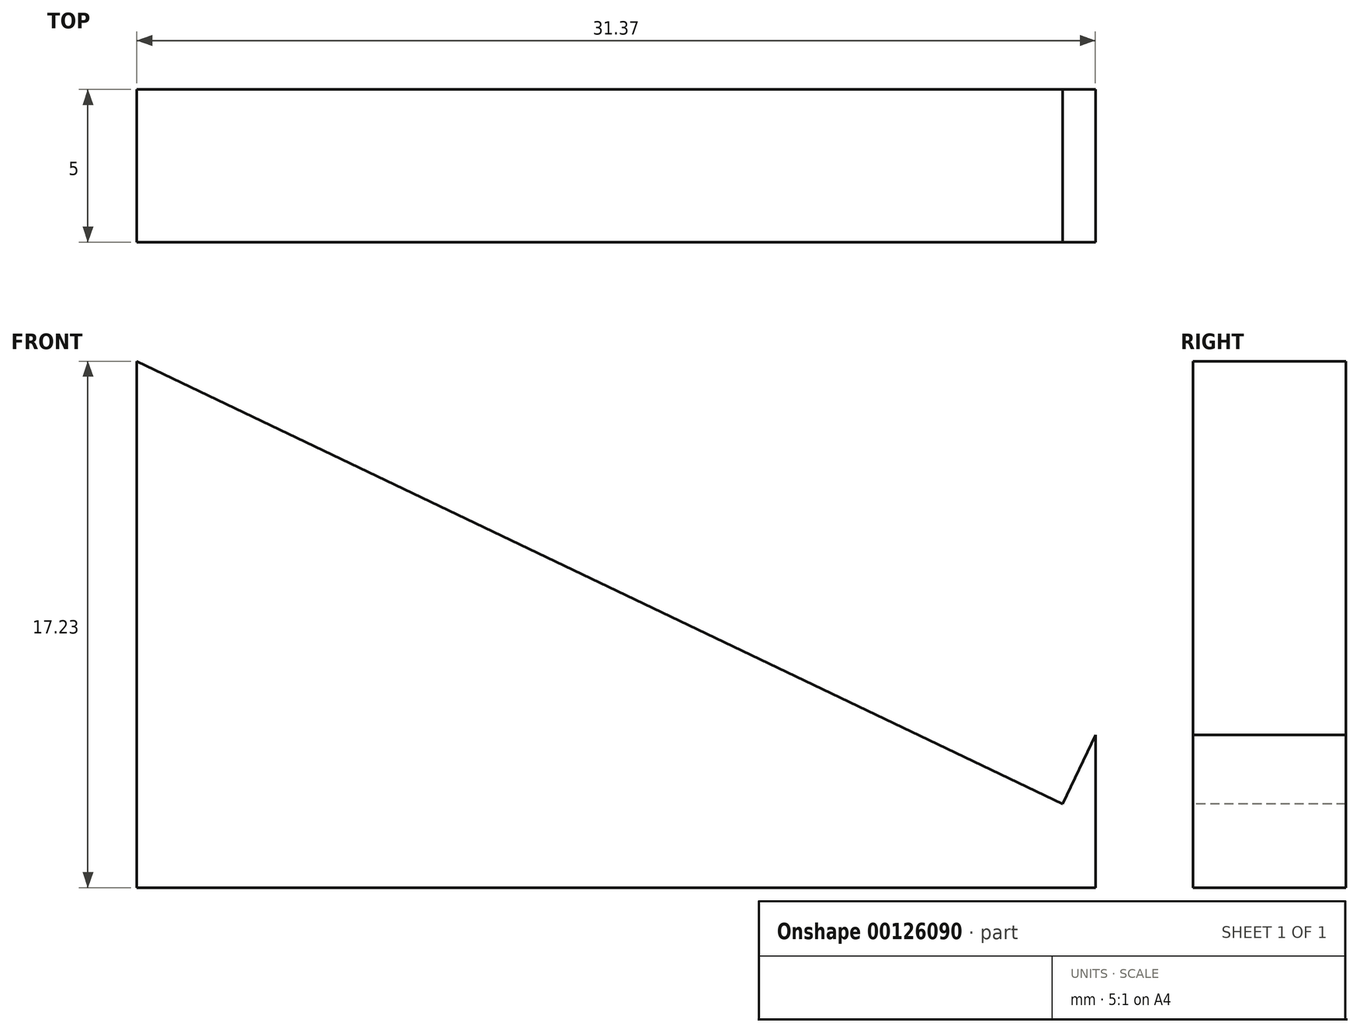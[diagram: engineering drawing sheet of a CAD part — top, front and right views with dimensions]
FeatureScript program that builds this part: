
annotation { "Feature Type Name" : "Feature", "Feature Type Description" : "" }
export const myFeature = defineFeature(function(context is Context, id is Id, definition is map)
    precondition{}
    {
        {
            var Q0;
            Q0=qCreatedBy(makeId("Front.planeOp"),FACE);
            var sketch = newSketch(context, id + "F0", { "sketchPlane" : qUnion([Q0])});
            skLineSegment(sketch, "E0", {"start": v(0, 0) * mm, "end": v(31.37, 0) * mm});
            skLineSegment(sketch, "E1", {"start": v(31.37, 0) * mm, "end": v(31.37, 5) * mm});
            skLineSegment(sketch, "E2", {"start": v(31.37, 5) * mm, "end": v(0, 20) * mm});
            skLineSegment(sketch, "E3", {"start": v(0, 20) * mm, "end": v(0, 0) * mm});
            skSolve(sketch);
        }
        {
            var Q0;
            Q0 = qSketchRegion(id + "F0", true);
            extrude(context, id + "F1", {"entities" : qUnion([Q0]), "oppositeDirection" : true, "depth" : 5 * mm});
        }
        {
            var Q0;
            Q0=makeQuery(id+"F1.opExtrude","SWEPT_FACE",FACE,{"disambiguationData":[OSD([sQuery(id+"F0.wireOp",EDGE,"E2")])]});
            extrude(context, id + "F2", {"entities" : qUnion([Q0]), "operationType" : NewBodyOperationType.REMOVE, "oppositeDirection" : true, "depth" : 2.5 * mm});
        }
    });
